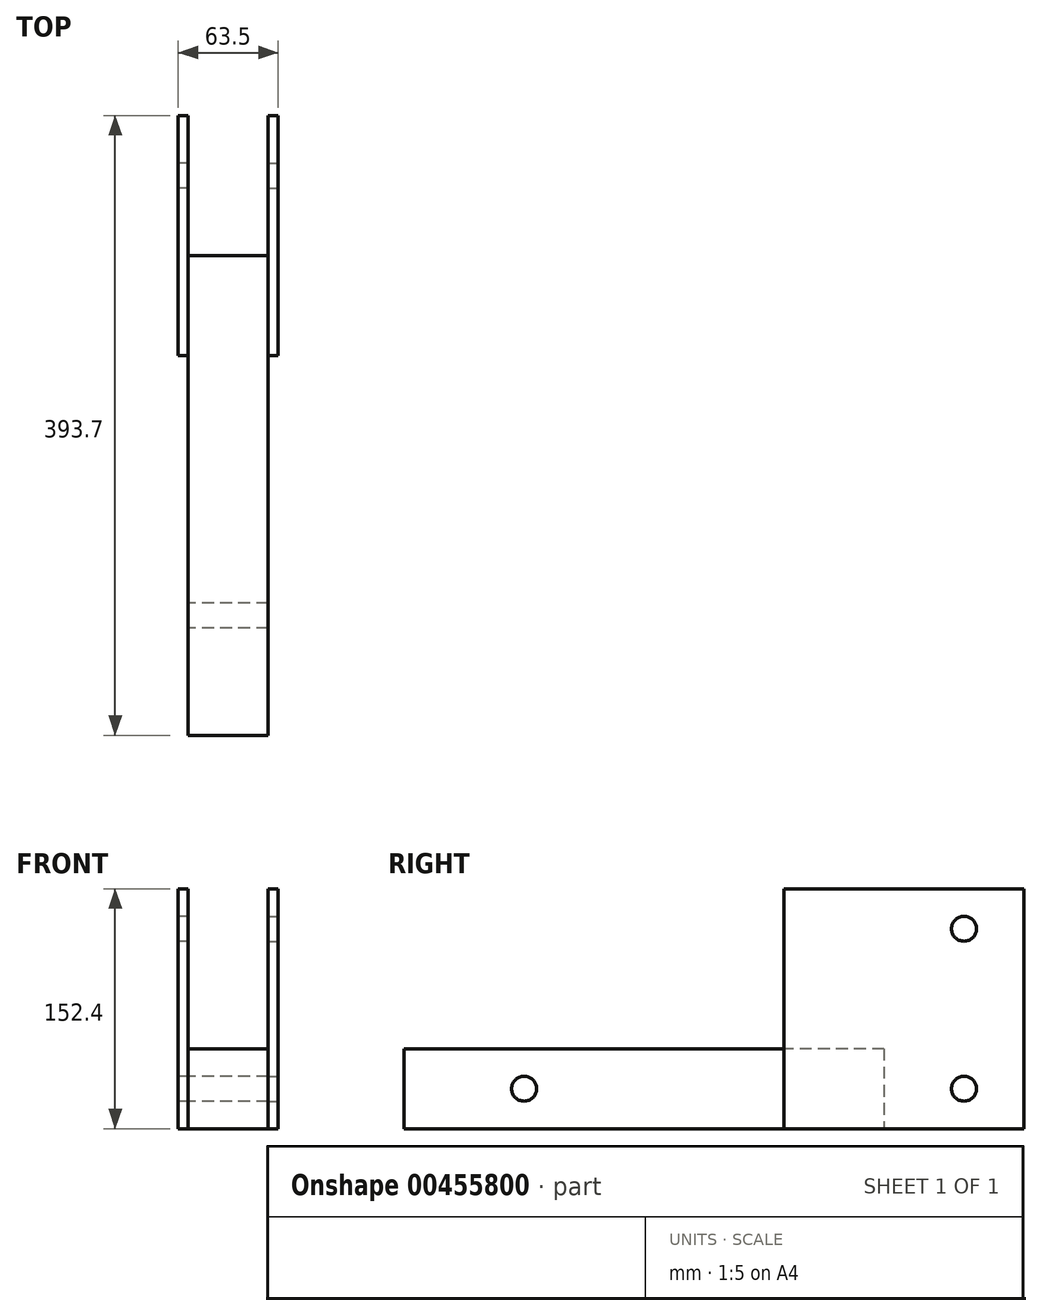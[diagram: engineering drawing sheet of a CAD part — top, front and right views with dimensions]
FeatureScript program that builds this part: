
annotation { "Feature Type Name" : "Feature", "Feature Type Description" : "" }
export const myFeature = defineFeature(function(context is Context, id is Id, definition is map)
    precondition{}
    {
        {
            var Q0;
            Q0=qCreatedBy(makeId("Top.planeOp"),FACE);
            var sketch = newSketch(context, id + "F0", { "sketchPlane" : qUnion([Q0])});
            skLineSegment(sketch, "E0.bottom", {"start": v(0, 0) * mm, "end": v(-50.8, 0) * mm});
            skLineSegment(sketch, "E0.top", {"start": v(0, -304.8) * mm, "end": v(-50.8, -304.8) * mm});
            skLineSegment(sketch, "E0.left", {"start": v(0, 0) * mm, "end": v(0, -304.8) * mm});
            skLineSegment(sketch, "E0.right", {"start": v(-50.8, 0) * mm, "end": v(-50.8, -304.8) * mm});
            skSolve(sketch);
        }
        {
            var Q0;
            Q0=makeQuery(id+"F0.imprint","IMPRINT",FACE,{"disambiguationData":[TD([[makeQuery(id+"F0.imprint","IMPRINT",EDGE,{"derivedFrom":sQuery(id+"F0.wireOp",EDGE,"E0.bottom")}),1.0]])]});
            extrude(context, id + "F1", {"entities" : qUnion([Q0]), "depth" : 50.8 * mm});
        }
        {
            var Q0;
            Q0=makeQuery(id+"F1.opExtrude","SWEPT_FACE",FACE,{"disambiguationData":[OSD([sQuery(id+"F0.wireOp",EDGE,"E0.right")])]});
            var sketch = newSketch(context, id + "F2", { "sketchPlane" : qUnion([Q0])});
            skLineSegment(sketch, "E1.bottom", {"start": v(63.5, 0) * mm, "end": v(-88.9, 0) * mm});
            skLineSegment(sketch, "E1.top", {"start": v(63.5, 152.4) * mm, "end": v(-88.9, 152.4) * mm});
            skLineSegment(sketch, "E1.left", {"start": v(63.5, 0) * mm, "end": v(63.5, 152.4) * mm});
            skLineSegment(sketch, "E1.right", {"start": v(-88.9, 0) * mm, "end": v(-88.9, 152.4) * mm});
            skSolve(sketch);
        }
        {
            var Q0;
            {var subQ2=sQuery(id+"F2.wireOp",EDGE,"E1.top");Q0=makeQuery(id+"F2.imprint","IMPRINT",FACE,{"disambiguationData":[TD([[makeQuery(id+"F2.imprint","IMPRINT",EDGE,{"derivedFrom":subQ2}),1.0]])]});}
            var Q1;
            {var subQ1=sQuery(id+"F0.wireOp",EDGE,"E0.right");var subQ2=makeQuery(id+"F1.opExtrude","SWEPT_EDGE",EDGE,{"disambiguationData":[OSD([sQuery(id+"F0.wireOp",EDGE,"E0.bottom"),subQ1])]});Q1=makeQuery(id+"F2.imprint","IMPRINT",FACE,{"disambiguationData":[TD([[makeQuery(id+"F2.imprint","IMPRINT",EDGE,{"derivedFrom":subQ2}),1.0]])]});}
            extrude(context, id + "F3", {"entities" : qUnion([Q0, Q1]), "operationType" : NewBodyOperationType.ADD, "depth" : 6.35 * mm});
        }
        {
            var Q0;
            Q0=makeQuery(id+"F3.opExtrude","CAP_FACE",FACE,{"disambiguationData":[OSD([sQuery(id+"F2.wireOp",EDGE,"E1.bottom"),sQuery(id+"F2.wireOp",EDGE,"E1.top"),sQuery(id+"F2.wireOp",EDGE,"E1.left"),sQuery(id+"F2.wireOp",EDGE,"E1.right")])],"isStart":false});
            var sketch = newSketch(context, id + "F4", { "sketchPlane" : qUnion([Q0])});
            skCircle(sketch, "E2", {"center": v(-50.8, 25.4) * mm, "radius": 7.94 * mm});
            skCircle(sketch, "E3", {"center": v(-50.8, 127) * mm, "radius": 7.94 * mm});
            skSolve(sketch);
        }
        {
            var Q0;
            Q0=makeQuery(id+"F4.imprint","IMPRINT",FACE,{"disambiguationData":[TD([[makeQuery(id+"F4.imprint","IMPRINT",EDGE,{"derivedFrom":sQuery(id+"F4.wireOp",EDGE,"E3")}),1.0]])]});
            var Q1;
            Q1=makeQuery(id+"F4.imprint","IMPRINT",FACE,{"disambiguationData":[TD([[makeQuery(id+"F4.imprint","IMPRINT",EDGE,{"derivedFrom":sQuery(id+"F4.wireOp",EDGE,"E2")}),1.0]])]});
            extrude(context, id + "F5", {"entities" : qUnion([Q0, Q1]), "operationType" : NewBodyOperationType.REMOVE, "oppositeDirection" : true, "depth" : 6.35 * mm});
        }
        {
            var Q0;
            Q0=makeQuery(id+"F1.opExtrude","SWEPT_FACE",FACE,{"disambiguationData":[OSD([sQuery(id+"F0.wireOp",EDGE,"E0.right")])]});
            var sketch = newSketch(context, id + "F6", { "sketchPlane" : qUnion([Q0])});
            skCircle(sketch, "E4", {"center": v(228.6, 25.4) * mm, "radius": 7.94 * mm});
            skSolve(sketch);
        }
        {
            var Q0;
            Q0=makeQuery(id+"F6.imprint","IMPRINT",FACE,{"disambiguationData":[TD([[makeQuery(id+"F6.imprint","IMPRINT",EDGE,{"derivedFrom":sQuery(id+"F6.wireOp",EDGE,"E4")}),1.0]])]});
            extrude(context, id + "F7", {"entities" : qUnion([Q0]), "operationType" : NewBodyOperationType.REMOVE, "oppositeDirection" : true, "depth" : 50.8 * mm});
        }
        {
            var Q0;
            Q0=makeQuery(id+"F1.opExtrude","SWEPT_FACE",FACE,{"disambiguationData":[OSD([sQuery(id+"F0.wireOp",EDGE,"E0.left")])]});
            var sketch = newSketch(context, id + "F8", { "sketchPlane" : qUnion([Q0])});
            skLineSegment(sketch, "E5.bottom", {"start": v(-63.5, 0) * mm, "end": v(88.9, 0) * mm});
            skLineSegment(sketch, "E5.top", {"start": v(-63.5, 152.4) * mm, "end": v(88.9, 152.4) * mm});
            skLineSegment(sketch, "E5.left", {"start": v(-63.5, 0) * mm, "end": v(-63.5, 152.4) * mm});
            skLineSegment(sketch, "E5.right", {"start": v(88.9, 0) * mm, "end": v(88.9, 152.4) * mm});
            skSolve(sketch);
        }
        {
            var Q0;
            {var subQ2=sQuery(id+"F8.wireOp",EDGE,"E5.top");Q0=makeQuery(id+"F8.imprint","IMPRINT",FACE,{"disambiguationData":[TD([[makeQuery(id+"F8.imprint","IMPRINT",EDGE,{"derivedFrom":subQ2}),-1.0]])]});}
            var Q1;
            {var subQ1=sQuery(id+"F0.wireOp",EDGE,"E0.left");var subQ2=makeQuery(id+"F1.opExtrude","SWEPT_EDGE",EDGE,{"disambiguationData":[OSD([sQuery(id+"F0.wireOp",EDGE,"E0.bottom"),subQ1])]});Q1=makeQuery(id+"F8.imprint","IMPRINT",FACE,{"disambiguationData":[TD([[makeQuery(id+"F8.imprint","IMPRINT",EDGE,{"derivedFrom":subQ2}),-1.0]])]});}
            extrude(context, id + "F9", {"entities" : qUnion([Q0, Q1]), "operationType" : NewBodyOperationType.ADD, "depth" : 6.35 * mm});
        }
        {
            var Q0;
            Q0=makeQuery(id+"F9.opExtrude","CAP_FACE",FACE,{"disambiguationData":[OSD([sQuery(id+"F8.wireOp",EDGE,"E5.bottom"),sQuery(id+"F8.wireOp",EDGE,"E5.top"),sQuery(id+"F8.wireOp",EDGE,"E5.left"),sQuery(id+"F8.wireOp",EDGE,"E5.right")])],"isStart":false});
            var sketch = newSketch(context, id + "F10", { "sketchPlane" : qUnion([Q0])});
            skCircle(sketch, "E6", {"center": v(50.8, 25.4) * mm, "radius": 7.94 * mm});
            skCircle(sketch, "E7", {"center": v(50.8, 127) * mm, "radius": 7.94 * mm});
            skSolve(sketch);
        }
        {
            var Q0;
            Q0=makeQuery(id+"F10.imprint","IMPRINT",FACE,{"disambiguationData":[TD([[makeQuery(id+"F10.imprint","IMPRINT",EDGE,{"derivedFrom":sQuery(id+"F10.wireOp",EDGE,"E7")}),1.0]])]});
            var Q1;
            Q1=makeQuery(id+"F10.imprint","IMPRINT",FACE,{"disambiguationData":[TD([[makeQuery(id+"F10.imprint","IMPRINT",EDGE,{"derivedFrom":sQuery(id+"F10.wireOp",EDGE,"E6")}),1.0]])]});
            extrude(context, id + "F11", {"entities" : qUnion([Q0, Q1]), "operationType" : NewBodyOperationType.REMOVE, "oppositeDirection" : true, "depth" : 6.35 * mm});
        }
    });
